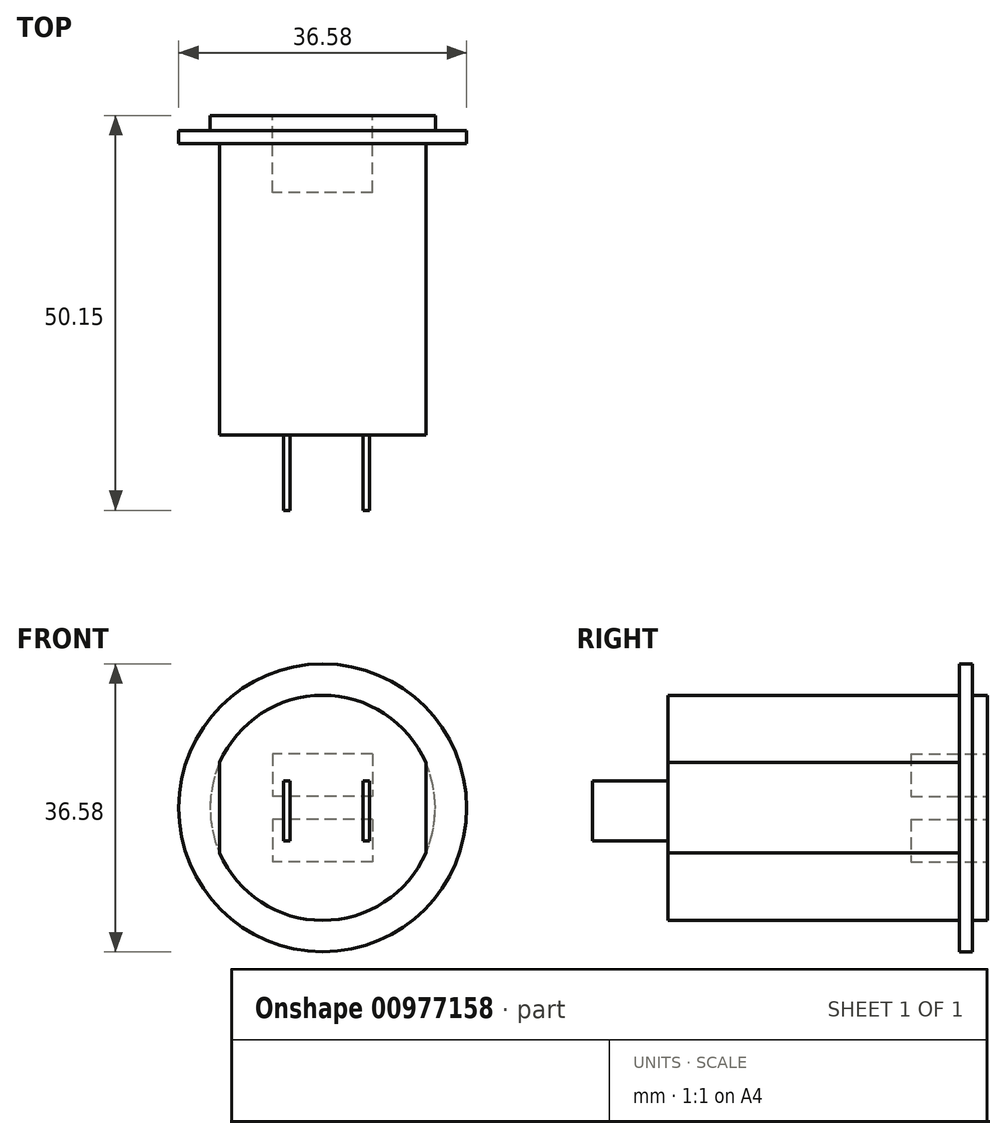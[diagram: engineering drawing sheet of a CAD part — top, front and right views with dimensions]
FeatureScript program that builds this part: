
annotation { "Feature Type Name" : "Feature", "Feature Type Description" : "" }
export const myFeature = defineFeature(function(context is Context, id is Id, definition is map)
    precondition{}
    {
        {
            var Q0;
            Q0=qCreatedBy(makeId("Front.planeOp"),FACE);
            var sketch = newSketch(context, id + "F0", { "sketchPlane" : qUnion([Q0])});
            skCircle(sketch, "E0", {"center": v(0, 0) * mm, "radius": 14.3 * mm});
            skSolve(sketch);
        }
        {
            var Q0;
            Q0 = qSketchRegion(id + "F0", true);
            extrude(context, id + "F1", {"entities" : qUnion([Q0]), "oppositeDirection" : true, "depth" : 40.6 * mm, "offsetDistance" : 25.4 * mm});
        }
        {
            var Q0;
            Q0=makeQuery(id+"F1.opExtrude","CAP_FACE",FACE,{"disambiguationData":[OSD([sQuery(id+"F0.wireOp",EDGE,"E0")])],"isStart":true});
            var sketch = newSketch(context, id + "F2", { "sketchPlane" : qUnion([Q0])});
            skLineSegment(sketch, "E1.left", {"start": v(-13.1, 22.3) * mm, "end": v(-13.1, -21.31) * mm});
            skLineSegment(sketch, "E1.right", {"start": v(13.1, 22.3) * mm, "end": v(13.1, -21.31) * mm});
            skLineSegment(sketch, "E2.bottom", {"start": v(-13.1, 22.3) * mm, "end": v(-24.96, 22.3) * mm});
            skLineSegment(sketch, "E2.top", {"start": v(-13.1, -21.31) * mm, "end": v(-24.96, -21.31) * mm});
            skLineSegment(sketch, "E2.right", {"start": v(-24.96, 22.3) * mm, "end": v(-24.96, -21.31) * mm});
            skLineSegment(sketch, "E3.bottom", {"start": v(13.1, 22.3) * mm, "end": v(23.44, 22.3) * mm});
            skLineSegment(sketch, "E3.top", {"start": v(13.1, -21.31) * mm, "end": v(23.44, -21.31) * mm});
            skLineSegment(sketch, "E3.right", {"start": v(23.44, 22.3) * mm, "end": v(23.44, -21.31) * mm});
            skSolve(sketch);
        }
        {
            var Q0;
            Q0 = qSketchRegion(id + "F2", true);
            extrude(context, id + "F3", {"entities" : qUnion([Q0]), "operationType" : NewBodyOperationType.REMOVE, "oppositeDirection" : true, "depth" : 37.08 * mm, "offsetDistance" : 25.4 * mm});
        }
        {
            var Q0;
            Q0=makeQuery(id+"F1.opExtrude","CAP_FACE",FACE,{"disambiguationData":[OSD([sQuery(id+"F0.wireOp",EDGE,"E0")])],"isStart":false});
            cPlane(context, id + "F4", {"entities" : qUnion([Q0]), "cplaneType" : CPlaneType.OFFSET, "offset" : 1.9 * mm, "oppositeDirection" : true, "width" : 152.4 * mm, "height" : 152.4 * mm});
        }
        {
            var Q0;
            Q0=qCreatedBy(id+"F4.planeOp",FACE);
            var sketch = newSketch(context, id + "F5", { "sketchPlane" : qUnion([Q0])});
            skCircle(sketch, "E4", {"center": v(0, 0) * mm, "radius": 18.29 * mm});
            skSolve(sketch);
        }
        {
            var Q0;
            Q0 = qSketchRegion(id + "F5", true);
            extrude(context, id + "F6", {"entities" : qUnion([Q0]), "operationType" : NewBodyOperationType.ADD, "oppositeDirection" : true, "depth" : 1.65 * mm, "offsetDistance" : 25.4 * mm});
        }
        {
            var Q0;
            Q0=makeQuery(id+"F1.opExtrude","CAP_FACE",FACE,{"disambiguationData":[OSD([sQuery(id+"F0.wireOp",EDGE,"E0")])],"isStart":false});
            var sketch = newSketch(context, id + "F7", { "sketchPlane" : qUnion([Q0])});
            skLineSegment(sketch, "E5.bottom", {"start": v(-6.35, 6.86) * mm, "end": v(6.35, 6.86) * mm});
            skLineSegment(sketch, "E5.top", {"start": v(-6.35, -6.86) * mm, "end": v(6.35, -6.86) * mm});
            skLineSegment(sketch, "E6.0", {"start": v(-13.1, 5.75) * mm, "end": v(-13.1, -5.75) * mm});
            skLineSegment(sketch, "E7.bottom", {"start": v(-6.35, 1.46) * mm, "end": v(6.35, 1.46) * mm});
            skLineSegment(sketch, "E7.top", {"start": v(-6.35, -1.46) * mm, "end": v(6.35, -1.46) * mm});
            skLineSegment(sketch, "E8", {"start": v(-6.35, 6.86) * mm, "end": v(-6.35, 1.46) * mm});
            skLineSegment(sketch, "E9", {"start": v(-6.35, -1.46) * mm, "end": v(-6.35, -6.86) * mm});
            skLineSegment(sketch, "E10", {"start": v(6.35, -1.46) * mm, "end": v(6.35, -6.86) * mm});
            skLineSegment(sketch, "E11", {"start": v(6.35, 6.86) * mm, "end": v(6.35, 1.46) * mm});
            skSolve(sketch);
        }
        {
            var Q0;
            Q0=makeQuery(id+"F7.imprint","IMPRINT",FACE,{"disambiguationData":[TD([[makeQuery(id+"F7.imprint","IMPRINT",EDGE,{"derivedFrom":sQuery(id+"F7.wireOp",EDGE,"E5.bottom")}),-1.0]])]});
            var Q1;
            Q1 = qSketchRegion(id + "F7", true);
            extrude(context, id + "F8", {"entities" : qUnion([Q0, Q1]), "operationType" : NewBodyOperationType.REMOVE, "oppositeDirection" : true, "depth" : 9.75 * mm, "offsetDistance" : 25.4 * mm});
        }
        {
            var Q0;
            Q0=makeQuery(id+"F1.opExtrude","CAP_FACE",FACE,{"disambiguationData":[OSD([sQuery(id+"F0.wireOp",EDGE,"E0")])],"isStart":true});
            var sketch = newSketch(context, id + "F9", { "sketchPlane" : qUnion([Q0])});
            skLineSegment(sketch, "E12.left", {"start": v(-4.97, 3.43) * mm, "end": v(-4.97, -4.2) * mm});
            skLineSegment(sketch, "E12.right", {"start": v(5.96, 3.43) * mm, "end": v(5.96, -4.2) * mm});
            skLineSegment(sketch, "E13.left", {"start": v(-4.18, 3.43) * mm, "end": v(-4.18, -4.2) * mm});
            skLineSegment(sketch, "E13.right", {"start": v(5.14, 3.43) * mm, "end": v(5.14, -4.2) * mm});
            skLineSegment(sketch, "E14", {"start": v(-4.97, 3.43) * mm, "end": v(-4.18, 3.43) * mm});
            skLineSegment(sketch, "E15", {"start": v(-4.97, -4.2) * mm, "end": v(-4.18, -4.2) * mm});
            skLineSegment(sketch, "E16.trimOffspring", {"start": v(5.14, 3.43) * mm, "end": v(5.96, 3.43) * mm});
            skLineSegment(sketch, "E17.trimOffspring", {"start": v(5.14, -4.2) * mm, "end": v(5.96, -4.2) * mm});
            skSolve(sketch);
        }
        {
            var Q0;
            Q0 = qSketchRegion(id + "F9", true);
            extrude(context, id + "F10", {"entities" : qUnion([Q0]), "operationType" : NewBodyOperationType.ADD, "depth" : 9.56 * mm, "offsetDistance" : 25.4 * mm});
        }
    });
